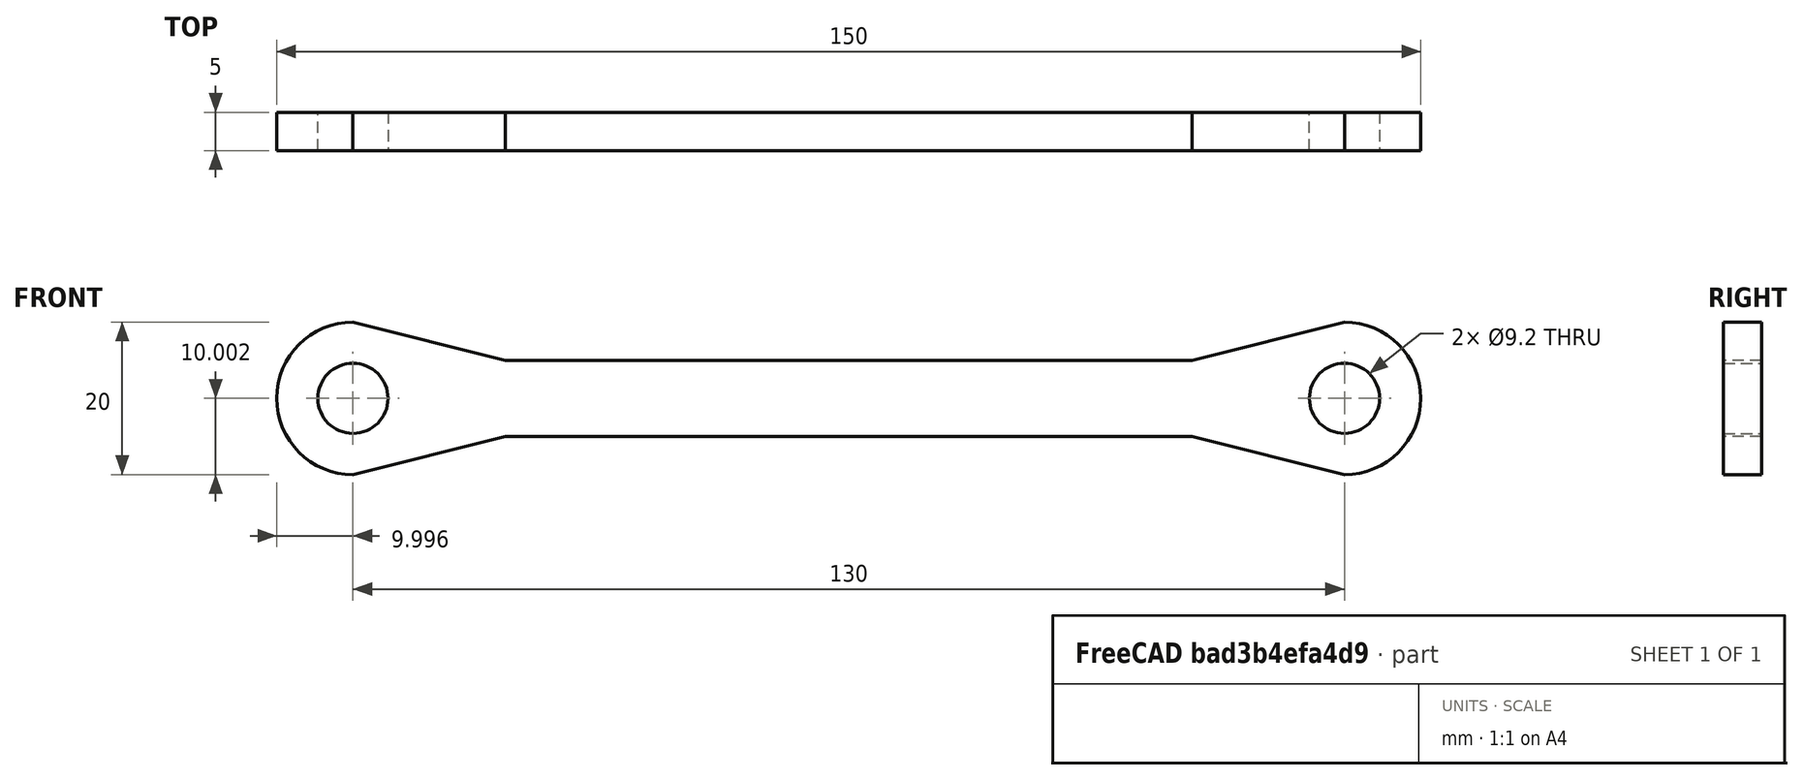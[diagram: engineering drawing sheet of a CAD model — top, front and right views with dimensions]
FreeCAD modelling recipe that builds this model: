
FCSTD DOCUMENT  (FreeCAD 0.16R6712 (Git))
Label: bras
License: All rights reserved
LicenseURL: http://en.wikipedia.org/wiki/All_rights_reserved
objects: Sketcher::SketchObject×1, PartDesign::Pad×1
note: 3 computed .brp shape members not serialized (recipe doc carries the construction recipe); baked Part::Feature solids carry a one-line shape summary decoded from their .brp

FEATURE [Sketcher::SketchObject] Sketch
  Placement = pos=(0,0,0) rot=(1,0,0;1.5708rad)
  sketch-geometry (10):
    g0: Circle CenterX=-59.4737 CenterY=0.241904 CenterZ=0 NormalX=0 NormalY=0 NormalZ=1 Radius=4.6
    g1: ArcOfCircle CenterX=-59.4737 CenterY=0.241904 CenterZ=0 NormalX=0 NormalY=0 NormalZ=1 Radius=10 StartAngle=4.71239 EndAngle=7.85398
    g2: Circle CenterX=-189.474 CenterY=0.241904 CenterZ=0 NormalX=0 NormalY=0 NormalZ=1 Radius=4.6
    g3: ArcOfCircle CenterX=-189.474 CenterY=0.241904 CenterZ=0 NormalX=0 NormalY=0 NormalZ=1 Radius=10 StartAngle=1.5708 EndAngle=4.71239
    g4: LineSegment StartX=-189.474 StartY=10.2419 StartZ=0 EndX=-169.474 EndY=5.2419 EndZ=0
    g5: LineSegment StartX=-169.474 StartY=5.2419 StartZ=0 EndX=-79.4737 EndY=5.2419 EndZ=0
    g6: LineSegment StartX=-79.4737 StartY=5.2419 StartZ=0 EndX=-59.4737 EndY=10.2419 EndZ=0
    g7: LineSegment StartX=-189.474 StartY=-9.7581 StartZ=0 EndX=-169.474 EndY=-4.7581 EndZ=0
    g8: LineSegment StartX=-169.474 StartY=-4.7581 StartZ=0 EndX=-79.4737 EndY=-4.7581 EndZ=0
    g9: LineSegment StartX=-79.4737 StartY=-4.7581 StartZ=0 EndX=-59.4737 EndY=-9.7581 EndZ=0
  constraints (28):
    c: Radius(g0) = 4.6
    c: Coincident(g1,g0)
    c: Radius(g1) = 10
    c: DistanceX(g1,g0) = 0
    c: DistanceX(g0,g1) = 0
    c: Radius(g2) = 4.6
    c: Coincident(g3,g2)
    c: Radius(g3) = 10
    c: DistanceX(g3,g2) = 0
    c: DistanceX(g3,g2) = 0
    c: DistanceY(g2,g0) = 0
    c: DistanceX(g2,g0) = 130
    c: Coincident(g4,g3)
    c: Coincident(g5,g4)
    c: Horizontal(g5)
    c: Coincident(g6,g5)
    c: Coincident(g6,g1)
    c: Coincident(g7,g3)
    c: Horizontal(g8)
    c: Coincident(g9,g1)
    c: Equal(g4,g7)
    c: Equal(g7,g6)
    c: Equal(g6,g9)
    c: Equal(g5,g8)
    c: DistanceY(g8,g4) = 10
    c: Coincident(g8,g7)
    c: Coincident(g8,g9)
    c: DistanceX(g4,g4) = 20
FEATURE [PartDesign::Pad] Pad001
  Length = 5
  Length2 = 100
  Placement = pos=(0,0,0) rot=(1,0,0;1.5708rad)
  Sketch = -> Sketch
  Type = 0
